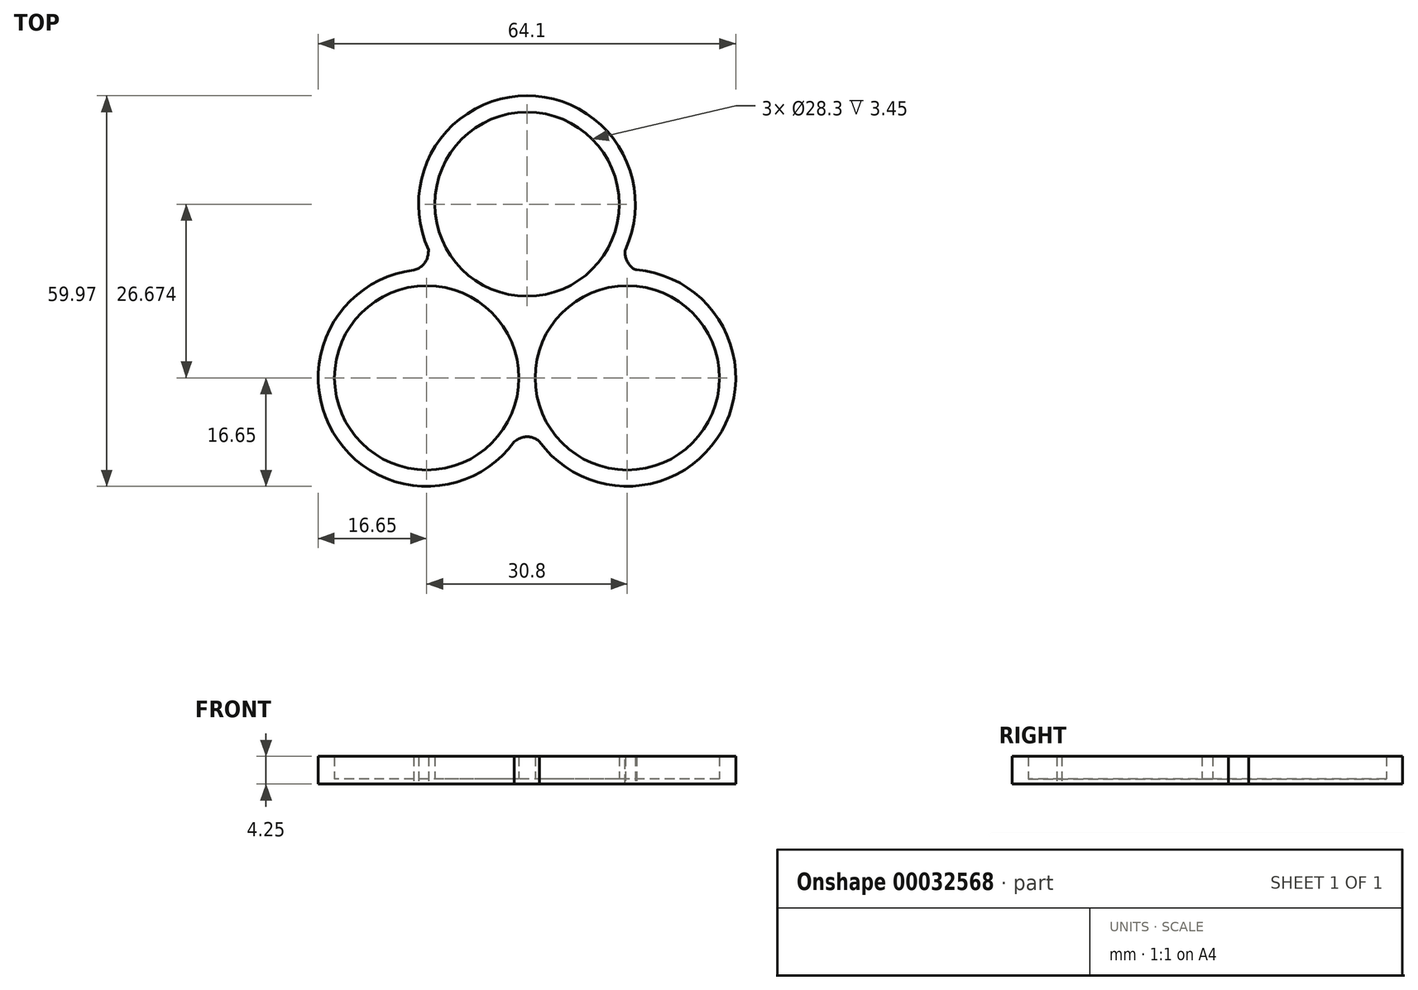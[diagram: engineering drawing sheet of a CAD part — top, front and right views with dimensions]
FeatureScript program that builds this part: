
annotation { "Feature Type Name" : "Feature", "Feature Type Description" : "" }
export const myFeature = defineFeature(function(context is Context, id is Id, definition is map)
    precondition{}
    {
        {
            var Q0;
            Q0=qCreatedBy(makeId("Top.planeOp"),FACE);
            var sketch = newSketch(context, id + "F0", { "sketchPlane" : qUnion([Q0])});
            skLineSegment(sketch, "E0", {"start": v(0, 26.67) * mm, "end": v(-15.4, 0) * mm, "construction": true});
            skLineSegment(sketch, "E1", {"start": v(0, 26.67) * mm, "end": v(15.4, 0) * mm, "construction": true});
            skLineSegment(sketch, "E2", {"start": v(15.4, 0) * mm, "end": v(-15.4, 0) * mm, "construction": true});
            skCircle(sketch, "E3", {"center": v(15.4, 0) * mm, "radius": 14.15 * mm});
            skCircle(sketch, "E4", {"center": v(0, 26.67) * mm, "radius": 14.15 * mm});
            skCircle(sketch, "E5", {"center": v(-15.4, 0) * mm, "radius": 14.15 * mm});
            skCircle(sketch, "E6", {"center": v(15.4, 0) * mm, "radius": 16.65 * mm});
            skCircle(sketch, "E7", {"center": v(0, 26.67) * mm, "radius": 16.65 * mm});
            skCircle(sketch, "E8", {"center": v(-15.4, 0) * mm, "radius": 16.65 * mm});
            skFitSpline(sketch, "E9", {"points": [v(-17.38, 16.53) * mm, v(-15.11, 19.68) * mm], "startDerivative": vector(4.75, 1.43) * mm, "endDerivative": vector(0.1, 4.63) * mm});
            skFitSpline(sketch, "E10", {"points": [v(15.11, 19.68) * mm, v(16.84, 16.59) * mm], "startDerivative": vector(-0.95, -3.29) * mm, "endDerivative": vector(3.42, -0.7) * mm});
            skFitSpline(sketch, "E11", {"points": [v(-1.94, -9.8) * mm, v(1.93, -9.79) * mm], "startDerivative": vector(3.79, 3) * mm, "endDerivative": vector(3.33, -2.94) * mm});
            skSolve(sketch);
        }
        {
            var Q0;
            {var subQ4=sQuery(id+"F0.wireOp",EDGE,"E5");var subQ6=sQuery(id+"F0.wireOp",EDGE,"E6");var subQ7=makeQuery(id+"F0.imprint","INTERSECT",VERTEX,{"derivedFrom":[subQ4,subQ6]});Q0=makeQuery(id+"F0.imprint","IMPRINT",FACE,{"disambiguationData":[TD([[makeQuery(id+"F0.imprint","IMPRINT",EDGE,{"disambiguationData":[TD([[subQ7,1.0]])],"derivedFrom":subQ4}),-1.0]])]});}
            var Q1;
            {var subQ5=sQuery(id+"F0.wireOp",EDGE,"E7");var subQ6=sQuery(id+"F0.wireOp",EDGE,"E3");var subQ7=makeQuery(id+"F0.imprint","INTERSECT",VERTEX,{"derivedFrom":[subQ6,subQ5]});Q1=makeQuery(id+"F0.imprint","IMPRINT",FACE,{"disambiguationData":[TD([[makeQuery(id+"F0.imprint","IMPRINT",EDGE,{"disambiguationData":[TD([[subQ7,1.0]])],"derivedFrom":subQ6}),-1.0]])]});}
            var Q2;
            {var subQ2=sQuery(id+"F0.wireOp",EDGE,"E6");var subQ7=sQuery(id+"F0.wireOp",EDGE,"E4");var subQ8=makeQuery(id+"F0.imprint","INTERSECT",VERTEX,{"derivedFrom":[subQ7,subQ2]});Q2=makeQuery(id+"F0.imprint","IMPRINT",FACE,{"disambiguationData":[TD([[makeQuery(id+"F0.imprint","IMPRINT",EDGE,{"disambiguationData":[TD([[subQ8,-1.0]])],"derivedFrom":subQ7}),-1.0]])]});}
            var Q3;
            {var subQ0=sQuery(id+"F0.wireOp",EDGE,"E3");var subQ1=makeQuery(id+"F0.imprint","INTERSECT",VERTEX,{"derivedFrom":[subQ0,sQuery(id+"F0.wireOp",EDGE,"E7")]});Q3=makeQuery(id+"F0.imprint","IMPRINT",FACE,{"disambiguationData":[TD([[makeQuery(id+"F0.imprint","IMPRINT",EDGE,{"disambiguationData":[TD([[subQ1,-1.0]])],"derivedFrom":subQ0}),1.0]])]});}
            var Q4;
            {var subQ0=sQuery(id+"F0.wireOp",EDGE,"E4");var subQ1=makeQuery(id+"F0.imprint","INTERSECT",VERTEX,{"derivedFrom":[subQ0,sQuery(id+"F0.wireOp",EDGE,"E6")]});Q4=makeQuery(id+"F0.imprint","IMPRINT",FACE,{"disambiguationData":[TD([[makeQuery(id+"F0.imprint","IMPRINT",EDGE,{"disambiguationData":[TD([[subQ1,1.0]])],"derivedFrom":subQ0}),1.0]])]});}
            var Q5;
            {var subQ0=sQuery(id+"F0.wireOp",EDGE,"E5");var subQ1=makeQuery(id+"F0.imprint","INTERSECT",VERTEX,{"derivedFrom":[subQ0,sQuery(id+"F0.wireOp",EDGE,"E6")]});Q5=makeQuery(id+"F0.imprint","IMPRINT",FACE,{"disambiguationData":[TD([[makeQuery(id+"F0.imprint","IMPRINT",EDGE,{"disambiguationData":[TD([[subQ1,-1.0]])],"derivedFrom":subQ0}),1.0]])]});}
            var Q6;
            {var subQ0=sQuery(id+"F0.wireOp",EDGE,"E10");Q6=makeQuery(id+"F0.imprint","IMPRINT",FACE,{"disambiguationData":[TD([[makeQuery(id+"F0.imprint","IMPRINT",EDGE,{"derivedFrom":subQ0}),-1.0]])]});}
            var Q7;
            {var subQ0=sQuery(id+"F0.wireOp",EDGE,"E11");Q7=makeQuery(id+"F0.imprint","IMPRINT",FACE,{"disambiguationData":[TD([[makeQuery(id+"F0.imprint","IMPRINT",EDGE,{"derivedFrom":subQ0}),1.0]])]});}
            var Q8;
            {var subQ0=sQuery(id+"F0.wireOp",EDGE,"E9");Q8=makeQuery(id+"F0.imprint","IMPRINT",FACE,{"disambiguationData":[TD([[makeQuery(id+"F0.imprint","IMPRINT",EDGE,{"derivedFrom":subQ0}),-1.0]])]});}
            var Q9;
            {var subQ0=sQuery(id+"F0.wireOp",EDGE,"E7");var subQ1=sQuery(id+"F0.wireOp",EDGE,"E6");var subQ2=makeQuery(id+"F0.imprint","INTERSECT",VERTEX,{"disambiguationData":[OD(1.0)],"derivedFrom":[subQ1,subQ0]});Q9=makeQuery(id+"F0.imprint","IMPRINT",FACE,{"disambiguationData":[TD([[makeQuery(id+"F0.imprint","IMPRINT",EDGE,{"disambiguationData":[TD([[subQ2,-1.0]])],"derivedFrom":subQ1}),-1.0]])]});}
            var Q10;
            {var subQ0=sQuery(id+"F0.wireOp",EDGE,"E7");var subQ1=sQuery(id+"F0.wireOp",EDGE,"E3");var subQ2=makeQuery(id+"F0.imprint","INTERSECT",VERTEX,{"derivedFrom":[subQ1,subQ0]});Q10=makeQuery(id+"F0.imprint","IMPRINT",FACE,{"disambiguationData":[TD([[makeQuery(id+"F0.imprint","IMPRINT",EDGE,{"disambiguationData":[TD([[subQ2,-1.0]])],"derivedFrom":subQ1}),-1.0]])]});}
            var Q11;
            {var subQ0=sQuery(id+"F0.wireOp",EDGE,"E6");var subQ1=sQuery(id+"F0.wireOp",EDGE,"E4");var subQ2=makeQuery(id+"F0.imprint","INTERSECT",VERTEX,{"derivedFrom":[subQ1,subQ0]});Q11=makeQuery(id+"F0.imprint","IMPRINT",FACE,{"disambiguationData":[TD([[makeQuery(id+"F0.imprint","IMPRINT",EDGE,{"disambiguationData":[TD([[subQ2,1.0]])],"derivedFrom":subQ1}),-1.0]])]});}
            var Q12;
            {var subQ0=sQuery(id+"F0.wireOp",EDGE,"E6");var subQ1=sQuery(id+"F0.wireOp",EDGE,"E5");var subQ2=makeQuery(id+"F0.imprint","INTERSECT",VERTEX,{"derivedFrom":[subQ1,subQ0]});Q12=makeQuery(id+"F0.imprint","IMPRINT",FACE,{"disambiguationData":[TD([[makeQuery(id+"F0.imprint","IMPRINT",EDGE,{"disambiguationData":[TD([[subQ2,-1.0]])],"derivedFrom":subQ1}),-1.0]])]});}
            var Q13;
            {var subQ0=sQuery(id+"F0.wireOp",EDGE,"E6");var subQ1=makeQuery(id+"F0.imprint","INTERSECT",VERTEX,{"derivedFrom":[sQuery(id+"F0.wireOp",EDGE,"E4"),subQ0]});Q13=makeQuery(id+"F0.imprint","IMPRINT",FACE,{"disambiguationData":[TD([[makeQuery(id+"F0.imprint","IMPRINT",EDGE,{"disambiguationData":[TD([[subQ1,1.0]])],"derivedFrom":subQ0}),1.0]])]});}
            var Q14;
            {var subQ0=sQuery(id+"F0.wireOp",EDGE,"E6");var subQ1=makeQuery(id+"F0.imprint","INTERSECT",VERTEX,{"derivedFrom":[sQuery(id+"F0.wireOp",EDGE,"E5"),subQ0]});Q14=makeQuery(id+"F0.imprint","IMPRINT",FACE,{"disambiguationData":[TD([[makeQuery(id+"F0.imprint","IMPRINT",EDGE,{"disambiguationData":[TD([[subQ1,1.0]])],"derivedFrom":subQ0}),1.0]])]});}
            var Q15;
            {var subQ0=sQuery(id+"F0.wireOp",EDGE,"E7");var subQ1=makeQuery(id+"F0.imprint","INTERSECT",VERTEX,{"derivedFrom":[sQuery(id+"F0.wireOp",EDGE,"E5"),subQ0]});Q15=makeQuery(id+"F0.imprint","IMPRINT",FACE,{"disambiguationData":[TD([[makeQuery(id+"F0.imprint","IMPRINT",EDGE,{"disambiguationData":[TD([[subQ1,1.0]])],"derivedFrom":subQ0}),1.0]])]});}
            extrude(context, id + "F1", {"entities" : qUnion([Q0, Q1, Q2, Q3, Q4, Q5, Q6, Q7, Q8, Q9, Q10, Q11, Q12, Q13, Q14, Q15]), "depth" : .8 * mm});
        }
        {
            var Q0;
            Q0 = qSketchRegion(id + "F0", true);
            var Q1;
            {var subQ0=sQuery(id+"F0.wireOp",EDGE,"E7");var subQ1=makeQuery(id+"F0.imprint","INTERSECT",VERTEX,{"derivedFrom":[sQuery(id+"F0.wireOp",EDGE,"E5"),subQ0]});Q1=makeQuery(id+"F0.imprint","IMPRINT",FACE,{"disambiguationData":[TD([[makeQuery(id+"F0.imprint","IMPRINT",EDGE,{"disambiguationData":[TD([[subQ1,1.0]])],"derivedFrom":subQ0}),1.0]])]});}
            var Q2;
            {var subQ0=sQuery(id+"F0.wireOp",EDGE,"E6");var subQ1=sQuery(id+"F0.wireOp",EDGE,"E5");var subQ2=makeQuery(id+"F0.imprint","INTERSECT",VERTEX,{"derivedFrom":[subQ1,subQ0]});Q2=makeQuery(id+"F0.imprint","IMPRINT",FACE,{"disambiguationData":[TD([[makeQuery(id+"F0.imprint","IMPRINT",EDGE,{"disambiguationData":[TD([[subQ2,-1.0]])],"derivedFrom":subQ1}),-1.0]])]});}
            var Q3;
            {var subQ0=sQuery(id+"F0.wireOp",EDGE,"E6");var subQ1=sQuery(id+"F0.wireOp",EDGE,"E4");var subQ2=makeQuery(id+"F0.imprint","INTERSECT",VERTEX,{"derivedFrom":[subQ1,subQ0]});Q3=makeQuery(id+"F0.imprint","IMPRINT",FACE,{"disambiguationData":[TD([[makeQuery(id+"F0.imprint","IMPRINT",EDGE,{"disambiguationData":[TD([[subQ2,1.0]])],"derivedFrom":subQ1}),-1.0]])]});}
            var Q4;
            {var subQ0=sQuery(id+"F0.wireOp",EDGE,"E6");var subQ1=makeQuery(id+"F0.imprint","INTERSECT",VERTEX,{"derivedFrom":[sQuery(id+"F0.wireOp",EDGE,"E4"),subQ0]});Q4=makeQuery(id+"F0.imprint","IMPRINT",FACE,{"disambiguationData":[TD([[makeQuery(id+"F0.imprint","IMPRINT",EDGE,{"disambiguationData":[TD([[subQ1,1.0]])],"derivedFrom":subQ0}),1.0]])]});}
            var Q5;
            {var subQ0=sQuery(id+"F0.wireOp",EDGE,"E7");var subQ1=sQuery(id+"F0.wireOp",EDGE,"E3");var subQ2=makeQuery(id+"F0.imprint","INTERSECT",VERTEX,{"derivedFrom":[subQ1,subQ0]});Q5=makeQuery(id+"F0.imprint","IMPRINT",FACE,{"disambiguationData":[TD([[makeQuery(id+"F0.imprint","IMPRINT",EDGE,{"disambiguationData":[TD([[subQ2,-1.0]])],"derivedFrom":subQ1}),-1.0]])]});}
            var Q6;
            {var subQ0=sQuery(id+"F0.wireOp",EDGE,"E6");var subQ1=makeQuery(id+"F0.imprint","INTERSECT",VERTEX,{"derivedFrom":[sQuery(id+"F0.wireOp",EDGE,"E5"),subQ0]});Q6=makeQuery(id+"F0.imprint","IMPRINT",FACE,{"disambiguationData":[TD([[makeQuery(id+"F0.imprint","IMPRINT",EDGE,{"disambiguationData":[TD([[subQ1,1.0]])],"derivedFrom":subQ0}),1.0]])]});}
            var Q7;
            {var subQ0=sQuery(id+"F0.wireOp",EDGE,"E7");var subQ1=sQuery(id+"F0.wireOp",EDGE,"E6");var subQ2=makeQuery(id+"F0.imprint","INTERSECT",VERTEX,{"disambiguationData":[OD(1.0)],"derivedFrom":[subQ1,subQ0]});Q7=makeQuery(id+"F0.imprint","IMPRINT",FACE,{"disambiguationData":[TD([[makeQuery(id+"F0.imprint","IMPRINT",EDGE,{"disambiguationData":[TD([[subQ2,-1.0]])],"derivedFrom":subQ1}),-1.0]])]});}
            extrude(context, id + "F2", {"entities" : qUnion([Q0, Q1, Q2, Q3, Q4, Q5, Q6, Q7]), "operationType" : NewBodyOperationType.ADD, "depth" : 4.25 * mm});
        }
    });
